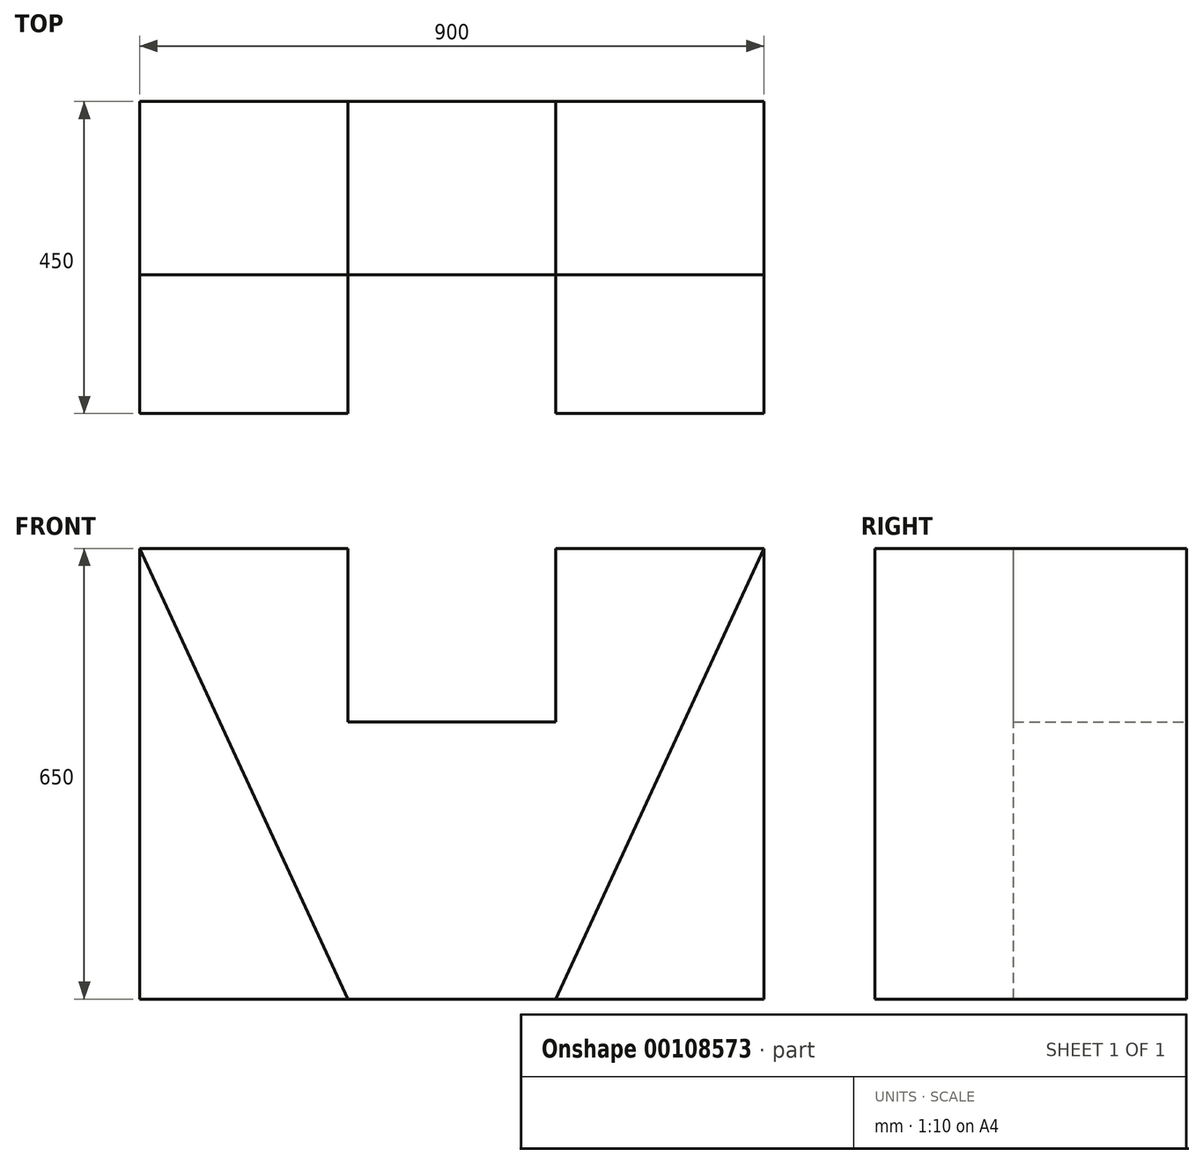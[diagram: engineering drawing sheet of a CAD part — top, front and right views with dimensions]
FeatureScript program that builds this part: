
annotation { "Feature Type Name" : "Feature", "Feature Type Description" : "" }
export const myFeature = defineFeature(function(context is Context, id is Id, definition is map)
    precondition{}
    {
        {
            var Q0;
            Q0=qCreatedBy(makeId("Front.planeOp"),FACE);
            var sketch = newSketch(context, id + "F0", { "sketchPlane" : qUnion([Q0])});
            skLineSegment(sketch, "E0.bottom", {"start": v(450, 325) * mm, "end": v(150, 325) * mm});
            skLineSegment(sketch, "E0.top", {"start": v(450, -325) * mm, "end": v(-450, -325) * mm});
            skLineSegment(sketch, "E0.left", {"start": v(450, 325) * mm, "end": v(450, -325) * mm});
            skLineSegment(sketch, "E0.right", {"start": v(-450, 325) * mm, "end": v(-450, -325) * mm});
            skPoint(sketch, "E0.middle", {"position": v(0, 0) * mm});
            skLineSegment(sketch, "E1.bottom", {"start": v(-150, 75) * mm, "end": v(150, 75) * mm});
            skLineSegment(sketch, "E1.left", {"start": v(-150, 75) * mm, "end": v(-150, 325) * mm});
            skLineSegment(sketch, "E1.right", {"start": v(150, 75) * mm, "end": v(150, 325) * mm});
            skPoint(sketch, "E1.middle", {"position": v(0, 325) * mm});
            skPoint(sketch, "E2.orphan", {"position": v(150, 575) * mm});
            skPoint(sketch, "E3.orphan", {"position": v(-150, 575) * mm});
            skLineSegment(sketch, "E4.trimOffspring", {"start": v(-150, 325) * mm, "end": v(-450, 325) * mm});
            skSolve(sketch);
        }
        {
            var Q0;
            Q0 = qSketchRegion(id + "F0", true);
            extrude(context, id + "F1", {"entities" : qUnion([Q0]), "depth" : 250 * mm});
        }
        {
            var Q0;
            Q0=makeQuery(id+"F1.opExtrude","CAP_FACE",FACE,{"disambiguationData":[OSD([sQuery(id+"F0.wireOp",EDGE,"E0.bottom"),sQuery(id+"F0.wireOp",EDGE,"E0.top"),sQuery(id+"F0.wireOp",EDGE,"E0.left"),sQuery(id+"F0.wireOp",EDGE,"E0.right"),sQuery(id+"F0.wireOp",EDGE,"E1.bottom"),sQuery(id+"F0.wireOp",EDGE,"E1.left"),sQuery(id+"F0.wireOp",EDGE,"E1.right"),sQuery(id+"F0.wireOp",EDGE,"E4.trimOffspring")])],"isStart":false});
            var sketch = newSketch(context, id + "F2", { "sketchPlane" : qUnion([Q0])});
            skLineSegment(sketch, "E5", {"start": v(-450, -325) * mm, "end": v(-150, -325) * mm});
            skLineSegment(sketch, "E6", {"start": v(450, -325) * mm, "end": v(150, -325) * mm});
            skLineSegment(sketch, "E7", {"start": v(150, -325) * mm, "end": v(450, 325) * mm});
            skLineSegment(sketch, "E8", {"start": v(-150, -325) * mm, "end": v(-450, 325) * mm});
            skSolve(sketch);
        }
        {
            var Q0;
            Q0 = qSketchRegion(id + "F2", true);
            var Q1;
            Q1=makeQuery(id+"F2.imprint","IMPRINT",FACE,{"disambiguationData":[TD([[makeQuery(id+"F2.imprint","IMPRINT",EDGE,{"derivedFrom":sQuery(id+"F2.wireOp",EDGE,"E5")}),-1.0]])]});
            var Q2;
            Q2=makeQuery(id+"F2.imprint","IMPRINT",FACE,{"disambiguationData":[TD([[makeQuery(id+"F2.imprint","IMPRINT",EDGE,{"derivedFrom":sQuery(id+"F2.wireOp",EDGE,"E6")}),-1.0]])]});
            extrude(context, id + "F3", {"entities" : qUnion([Q0, Q1, Q2]), "operationType" : NewBodyOperationType.ADD, "depth" : 200 * mm});
        }
    });
